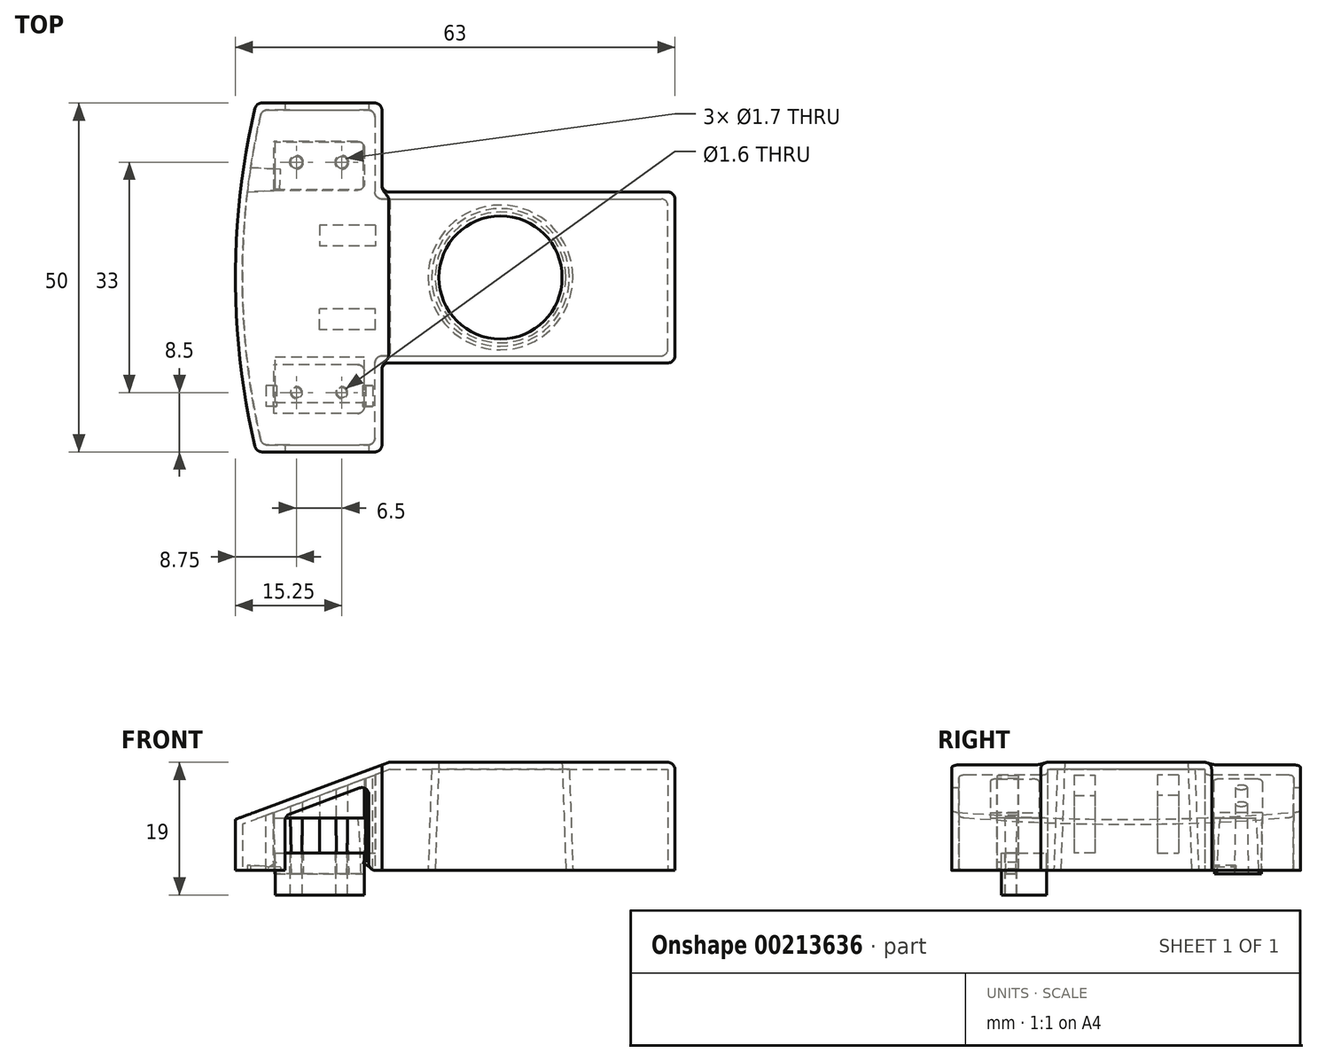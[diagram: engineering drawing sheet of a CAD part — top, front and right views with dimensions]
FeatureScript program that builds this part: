
annotation { "Feature Type Name" : "Feature", "Feature Type Description" : "" }
export const myFeature = defineFeature(function(context is Context, id is Id, definition is map)
    precondition{}
    {
        {
            var Q0;
            Q0=qCreatedBy(makeId("Top.planeOp"),FACE);
            var sketch = newSketch(context, id + "F0", { "sketchPlane" : qUnion([Q0])});
            skCircle(sketch, "E0", {"center": v(-4, 0) * mm, "radius": 9.37 * mm});
            skLineSegment(sketch, "E1.bottom", {"start": v(-21, -12.25) * mm, "end": v(21, -12.25) * mm});
            skLineSegment(sketch, "E1.top", {"start": v(-21, 12.25) * mm, "end": v(21, 12.25) * mm});
            skLineSegment(sketch, "E1.right", {"start": v(21, -12.25) * mm, "end": v(21, 12.25) * mm});
            skLineSegment(sketch, "E2.bottom", {"start": v(-21, -25) * mm, "end": v(-39, -25) * mm});
            skLineSegment(sketch, "E2.top", {"start": v(-21, 25) * mm, "end": v(-39, 25) * mm});
            skLineSegment(sketch, "E2.left", {"start": v(-21, -25) * mm, "end": v(-21, -12.25) * mm});
            skLineSegment(sketch, "E2.right", {"start": v(-39, -25) * mm, "end": v(-39, 25) * mm});
            skPoint(sketch, "E2.middle", {"position": v(-30, 0) * mm});
            skLineSegment(sketch, "E3.trimOffspring", {"start": v(-21, 12.25) * mm, "end": v(-21, 25) * mm});
            skLineSegment(sketch, "E4", {"start": v(-20, 12.25) * mm, "end": v(-20, -12.25) * mm});
            skPoint(sketch, "E5", {"position": v(-42, 0) * mm});
            skPoint(sketch, "E5.positionSnap0", {"position": v(-39, 0) * mm});
            skArc(sketch, "E6", {"start": v(-39, 25) * mm, "mid": v(-42, 0) * mm, "end": v(-39, -25) * mm});
            skSolve(sketch);
        }
        {
            var Q0;
            Q0=qSketchRegion(id+"F0",true);
            var Q1;
            Q1=makeQuery(id+"F0.imprint","IMPRINT",FACE,{"disambiguationData":[TD([[makeQuery(id+"F0.imprint","IMPRINT",EDGE,{"derivedFrom":sQuery(id+"F0.wireOp",EDGE,"E0")}),1.0]])]});
            extrude(context, id + "F1", {"entities" : qUnion([Q0, Q1]), "depth" : 15.5 * mm});
        }
        {
            var Q0;
            Q0=makeQuery(id+"F0.imprint","IMPRINT",FACE,{"disambiguationData":[TD([[makeQuery(id+"F0.imprint","IMPRINT",EDGE,{"derivedFrom":sQuery(id+"F0.wireOp",EDGE,"E0")}),1.0]])]});
            var Q1;
            Q1=makeQuery(id+"F1.opExtrude","CAP_FACE",FACE,{"disambiguationData":[OSD([sQuery(id+"F0.wireOp",EDGE,"E1.bottom"),sQuery(id+"F0.wireOp",EDGE,"E1.top"),sQuery(id+"F0.wireOp",EDGE,"E1.right"),sQuery(id+"F0.wireOp",EDGE,"E2.bottom"),sQuery(id+"F0.wireOp",EDGE,"E2.top"),sQuery(id+"F0.wireOp",EDGE,"E2.left"),sQuery(id+"F0.wireOp",EDGE,"E3.trimOffspring"),sQuery(id+"F0.wireOp",EDGE,"E6")])],"isStart":false});
            extrude(context, id + "F2", {"entities" : qUnion([Q0]), "operationType" : NewBodyOperationType.REMOVE, "endBound" : BoundingType.UP_TO_SURFACE, "endBoundEntityFace" : qUnion([Q1]), "depth" : 25 * mm, "hasDraft" : true, "draftAngle" : 2 * degree, "draftPullDirection" : true});
        }
        {
            var Q0;
            Q0=qCreatedBy(makeId("Front.planeOp"),FACE);
            var Q1;
            Q1=makeQuery(id+"F1.opExtrude","CAP_EDGE",EDGE,{"disambiguationData":[OSD([sQuery(id+"F0.wireOp",EDGE,"E2.bottom")])],"isStart":true});
            cPlane(context, id + "F3", {"entities" : qUnion([Q0, Q1]), "cplaneType" : CPlaneType.LINE_ANGLE, "offset" : 25 * mm, "angle" : 0 * degree, "width" : 150 * mm, "height" : 150 * mm});
        }
        {
            var Q0;
            Q0=qCreatedBy(id+"F3.planeOp",FACE);
            var sketch = newSketch(context, id + "F4", { "sketchPlane" : qUnion([Q0])});
            skLineSegment(sketch, "E7", {"start": v(20, 15.5) * mm, "end": v(42, 15.5) * mm});
            skLineSegment(sketch, "E8", {"start": v(42, 15.5) * mm, "end": v(42, 7.32) * mm});
            skLineSegment(sketch, "E9", {"start": v(42, 7.32) * mm, "end": v(20, 15.5) * mm});
            skLineSegment(sketch, "E10", {"start": v(42, 0) * mm, "end": v(41.46, 15.5) * mm, "construction": true});
            skLineSegment(sketch, "E11", {"start": v(42, 0) * mm, "end": v(42, 27.73) * mm, "construction": true});
            skSolve(sketch);
        }
        {
            var Q0;
            Q0=qSketchRegion(id+"F4",true);
            extrude(context, id + "F5", {"entities" : qUnion([Q0]), "operationType" : NewBodyOperationType.REMOVE, "endBound" : BoundingType.THROUGH_ALL, "depth" : 25 * mm});
        }
        {
            var Q0;
            Q0=makeQuery(id+"F1.opExtrude","CAP_FACE",FACE,{"disambiguationData":[OSD([sQuery(id+"F0.wireOp",EDGE,"E1.bottom"),sQuery(id+"F0.wireOp",EDGE,"E1.top"),sQuery(id+"F0.wireOp",EDGE,"E1.right"),sQuery(id+"F0.wireOp",EDGE,"E2.bottom"),sQuery(id+"F0.wireOp",EDGE,"E2.top"),sQuery(id+"F0.wireOp",EDGE,"E2.left"),sQuery(id+"F0.wireOp",EDGE,"E3.trimOffspring"),sQuery(id+"F0.wireOp",EDGE,"E6")])],"isStart":true});
            shell(context, id + "F6", {"entities" : qUnion([Q0]), "thickness" : 1 * mm});
        }
        {
            var Q0;
            Q0=makeQuery(id+"F1.opExtrude","SWEPT_FACE",FACE,{"disambiguationData":[OSD([sQuery(id+"F0.wireOp",EDGE,"E2.bottom")])]});
            var sketch = newSketch(context, id + "F7", { "sketchPlane" : qUnion([Q0])});
            skLineSegment(sketch, "E12", {"start": v(-20, 15.5) * mm, "end": v(-39, 8.43) * mm});
            skLineSegment(sketch, "E13", {"start": v(-39, 8.43) * mm, "end": v(-39, 15.5) * mm});
            skLineSegment(sketch, "E14", {"start": v(-39, 15.5) * mm, "end": v(-20, 15.5) * mm});
            skLineSegment(sketch, "E15", {"start": v(-34.87, 0) * mm, "end": v(-34.87, 7.86) * mm});
            skLineSegment(sketch, "E16", {"start": v(-34.87, 7.86) * mm, "end": v(-22.87, 12.32) * mm});
            skLineSegment(sketch, "E17", {"start": v(-22.87, 0) * mm, "end": v(-34.87, 0) * mm});
            skLineSegment(sketch, "E18", {"start": v(-22.87, 12.32) * mm, "end": v(-22.87, 0) * mm});
            skSolve(sketch);
        }
        {
            var Q0;
            Q0=makeQuery(id+"F7.imprint","IMPRINT",FACE,{"disambiguationData":[TD([[makeQuery(id+"F7.imprint","IMPRINT",EDGE,{"derivedFrom":sQuery(id+"F7.wireOp",EDGE,"E15")}),-1.0]])]});
            extrude(context, id + "F8", {"entities" : qUnion([Q0]), "operationType" : NewBodyOperationType.REMOVE, "endBound" : BoundingType.THROUGH_ALL, "oppositeDirection" : true, "depth" : 25 * mm});
        }
        {
            var Q0;
            Q0=makeQuery(id+"F1.opExtrude","CAP_FACE",FACE,{"disambiguationData":[OSD([sQuery(id+"F0.wireOp",EDGE,"E0"),sQuery(id+"F0.wireOp",EDGE,"E1.bottom"),sQuery(id+"F0.wireOp",EDGE,"E1.top"),sQuery(id+"F0.wireOp",EDGE,"E1.right"),sQuery(id+"F0.wireOp",EDGE,"E2.bottom"),sQuery(id+"F0.wireOp",EDGE,"E2.top"),sQuery(id+"F0.wireOp",EDGE,"E2.left"),sQuery(id+"F0.wireOp",EDGE,"E2.right"),sQuery(id+"F0.wireOp",EDGE,"E3.trimOffspring")])],"isStart":false});
            cPlane(context, id + "F9", {"entities" : qUnion([Q0]), "cplaneType" : CPlaneType.OFFSET, "offset" : 8 * mm, "oppositeDirection" : true, "width" : 150 * mm, "height" : 150 * mm});
        }
        {
            var Q0;
            Q0=qCreatedBy(id+"F9.planeOp",FACE);
            var sketch = newSketch(context, id + "F10", { "sketchPlane" : qUnion([Q0])});
            skLineSegment(sketch, "E19", {"start": v(0, 0) * mm, "end": v(-63, 0) * mm, "construction": true});
            skLineSegment(sketch, "E20.bottom", {"start": v(-36.5, -12.5) * mm, "end": v(-23.5, -12.5) * mm});
            skLineSegment(sketch, "E20.top", {"start": v(-36.5, -19.5) * mm, "end": v(-23.5, -19.5) * mm});
            skLineSegment(sketch, "E20.left", {"start": v(-36.5, -12.5) * mm, "end": v(-36.5, -19.5) * mm});
            skLineSegment(sketch, "E20.right", {"start": v(-23.5, -12.5) * mm, "end": v(-23.5, -19.5) * mm});
            skPoint(sketch, "E20.middle", {"position": v(-30, -16) * mm});
            skPoint(sketch, "E21", {"position": v(-33.25, -16.5) * mm});
            skPoint(sketch, "E22", {"position": v(-26.75, -16.5) * mm});
            skCircle(sketch, "E23", {"center": v(-33.25, -16.5) * mm, "radius": 0.85 * mm});
            skCircle(sketch, "E24", {"center": v(-26.75, -16.5) * mm, "radius": 0.85 * mm});
            skLineSegment(sketch, "E25.MirrorCS", {"start": v(-36.5, 12.5) * mm, "end": v(-23.5, 12.5) * mm});
            skLineSegment(sketch, "E26.MirrorCS", {"start": v(-36.5, 12.5) * mm, "end": v(-36.5, 19.5) * mm});
            skLineSegment(sketch, "E27.MirrorCS", {"start": v(-36.5, 19.5) * mm, "end": v(-23.5, 19.5) * mm});
            skLineSegment(sketch, "E28.MirrorCS", {"start": v(-23.5, 12.5) * mm, "end": v(-23.5, 19.5) * mm});
            skCircle(sketch, "E29.MirrorC", {"center": v(-26.75, 16.5) * mm, "radius": 0.85 * mm});
            skCircle(sketch, "E30.MirrorC", {"center": v(-33.25, 16.5) * mm, "radius": 0.85 * mm});
            skSolve(sketch);
        }
        {
            var Q0;
            Q0=makeQuery(id+"F10.imprint","IMPRINT",FACE,{"disambiguationData":[TD([[makeQuery(id+"F10.imprint","IMPRINT",EDGE,{"derivedFrom":sQuery(id+"F10.wireOp",EDGE,"E20.bottom")}),-1.0]])]});
            var Q1;
            Q1=makeQuery(id+"F10.imprint","IMPRINT",FACE,{"disambiguationData":[TD([[makeQuery(id+"F10.imprint","IMPRINT",EDGE,{"derivedFrom":sQuery(id+"F10.wireOp",EDGE,"E23")}),1.0]])]});
            var Q2;
            Q2=makeQuery(id+"F10.imprint","IMPRINT",FACE,{"disambiguationData":[TD([[makeQuery(id+"F10.imprint","IMPRINT",EDGE,{"derivedFrom":sQuery(id+"F10.wireOp",EDGE,"E24")}),1.0]])]});
            var Q3;
            Q3=makeQuery(id+"F10.imprint","IMPRINT",FACE,{"disambiguationData":[TD([[makeQuery(id+"F10.imprint","IMPRINT",EDGE,{"derivedFrom":sQuery(id+"F10.wireOp",EDGE,"E25.MirrorCS")}),1.0]])]});
            var Q4;
            Q4=makeQuery(id+"F10.imprint","IMPRINT",FACE,{"disambiguationData":[TD([[makeQuery(id+"F10.imprint","IMPRINT",EDGE,{"derivedFrom":sQuery(id+"F10.wireOp",EDGE,"E30.MirrorC")}),-1.0]])]});
            var Q5;
            Q5=makeQuery(id+"F10.imprint","IMPRINT",FACE,{"disambiguationData":[TD([[makeQuery(id+"F10.imprint","IMPRINT",EDGE,{"derivedFrom":sQuery(id+"F10.wireOp",EDGE,"E29.MirrorC")}),-1.0]])]});
            var Q6;
            Q6=makeQuery(id+"F6.opShell","OFFSET_FACE",FACE,{"disambiguationData":[OSD([sQuery(id+"F4.wireOp",EDGE,"E9")])]});
            extrude(context, id + "F11", {"entities" : qUnion([Q0, Q1, Q2, Q3, Q4, Q5]), "operationType" : NewBodyOperationType.ADD, "endBound" : BoundingType.UP_TO_SURFACE, "endBoundEntityFace" : qUnion([Q6]), "depth" : 25 * mm});
        }
        {
            var Q0;
            Q0=makeQuery(id+"F10.imprint","IMPRINT",FACE,{"disambiguationData":[TD([[makeQuery(id+"F10.imprint","IMPRINT",EDGE,{"derivedFrom":sQuery(id+"F10.wireOp",EDGE,"E23")}),1.0]])]});
            var Q1;
            Q1=makeQuery(id+"F10.imprint","IMPRINT",FACE,{"disambiguationData":[TD([[makeQuery(id+"F10.imprint","IMPRINT",EDGE,{"derivedFrom":sQuery(id+"F10.wireOp",EDGE,"E29.MirrorC")}),-1.0]])]});
            var Q2;
            Q2=makeQuery(id+"F10.imprint","IMPRINT",FACE,{"disambiguationData":[TD([[makeQuery(id+"F10.imprint","IMPRINT",EDGE,{"derivedFrom":sQuery(id+"F10.wireOp",EDGE,"E30.MirrorC")}),-1.0]])]});
            var Q3;
            Q3=makeQuery(id+"F10.imprint","IMPRINT",FACE,{"disambiguationData":[TD([[makeQuery(id+"F10.imprint","IMPRINT",EDGE,{"derivedFrom":sQuery(id+"F10.wireOp",EDGE,"E24")}),1.0]])]});
            extrude(context, id + "F12", {"entities" : qUnion([Q0, Q1, Q2, Q3]), "operationType" : NewBodyOperationType.ADD, "oppositeDirection" : true, "depth" : 8 * mm, "hasDraft" : true, "draftAngle" : 1 * degree, "draftPullDirection" : true});
        }
        {
            var Q0;
            Q0=makeQuery(id+"F1.opExtrude","CAP_EDGE",EDGE,{"disambiguationData":[OSD([sQuery(id+"F0.wireOp",EDGE,"E1.bottom")])],"isStart":false});
            var Q1;
            Q1=makeQuery(id+"F1.opExtrude","CAP_EDGE",EDGE,{"disambiguationData":[OSD([sQuery(id+"F0.wireOp",EDGE,"E1.right")])],"isStart":false});
            var Q2;
            Q2=makeQuery(id+"F1.opExtrude","CAP_EDGE",EDGE,{"disambiguationData":[OSD([sQuery(id+"F0.wireOp",EDGE,"E1.top")])],"isStart":false});
            var Q3;
            Q3=makeQuery(id+"F1.opExtrude","SWEPT_EDGE",EDGE,{"disambiguationData":[OSD([sQuery(id+"F0.wireOp",EDGE,"E1.bottom"),sQuery(id+"F0.wireOp",EDGE,"E1.right")])]});
            var Q4;
            Q4=makeQuery(id+"F1.opExtrude","SWEPT_EDGE",EDGE,{"disambiguationData":[OSD([sQuery(id+"F0.wireOp",EDGE,"E1.top"),sQuery(id+"F0.wireOp",EDGE,"E1.right")])]});
            fillet(context, id + "F13", {"entities" : qUnion([Q0, Q1, Q2, Q3, Q4]), "radius" : 1 * mm, "tangentPropagation" : true, "allowEdgeOverflow" : false});
        }
        {
            var Q0;
            Q0=makeQuery(id+"F1.opExtrude","SWEPT_EDGE",EDGE,{"disambiguationData":[OSD([sQuery(id+"F0.wireOp",EDGE,"E2.bottom"),sQuery(id+"F0.wireOp",EDGE,"E2.left")])]});
            var Q1;
            Q1=makeQuery(id+"F5.boolean.opBoolean","INTERSECT",EDGE,{"derivedFrom":[makeQuery(id+"F1.opExtrude","SWEPT_FACE",FACE,{"disambiguationData":[OSD([sQuery(id+"F0.wireOp",EDGE,"E2.left")])]}),makeQuery(id+"F5.opExtrude","SWEPT_FACE",FACE,{"disambiguationData":[OSD([sQuery(id+"FjstzwEYRuGCUyq_1.wireOp",EDGE,"6156deb2-2619-4c56-9df6-34b3699534c4")])]})]});
            var Q2;
            Q2=makeQuery(id+"F5.boolean.opBoolean","COPY",EDGE,{"derivedFrom":makeQuery(id+"F5.opExtrude","CAP_EDGE",EDGE,{"disambiguationData":[OSD([sQuery(id+"FjstzwEYRuGCUyq_1.wireOp",EDGE,"6156deb2-2619-4c56-9df6-34b3699534c4")])],"isStart":true})});
            var Q3;
            Q3=makeQuery(id+"F1.opExtrude","SWEPT_EDGE",EDGE,{"disambiguationData":[OSD([sQuery(id+"F0.wireOp",EDGE,"E2.bottom"),sQuery(id+"F0.wireOp",EDGE,"E2.right"),sQuery(id+"F0.wireOp",EDGE,"E6")])]});
            var Q4;
            Q4=makeQuery(id+"F5.boolean.opBoolean","INTERSECT",EDGE,{"derivedFrom":[makeQuery(id+"F1.opExtrude","SWEPT_FACE",FACE,{"disambiguationData":[OSD([sQuery(id+"F0.wireOp",EDGE,"E6")])]}),makeQuery(id+"F5.opExtrude","SWEPT_FACE",FACE,{"disambiguationData":[OSD([sQuery(id+"FjstzwEYRuGCUyq_1.wireOp",EDGE,"6156deb2-2619-4c56-9df6-34b3699534c4")])]})]});
            var Q5;
            Q5=makeQuery(id+"F5.boolean.opBoolean","INTERSECT",EDGE,{"derivedFrom":[makeQuery(id+"F1.opExtrude","SWEPT_FACE",FACE,{"disambiguationData":[OSD([sQuery(id+"F0.wireOp",EDGE,"E2.top")])]}),makeQuery(id+"F5.opExtrude","SWEPT_FACE",FACE,{"disambiguationData":[OSD([sQuery(id+"FjstzwEYRuGCUyq_1.wireOp",EDGE,"6156deb2-2619-4c56-9df6-34b3699534c4")])]})]});
            var Q6;
            Q6=makeQuery(id+"F1.opExtrude","SWEPT_EDGE",EDGE,{"disambiguationData":[OSD([sQuery(id+"F0.wireOp",EDGE,"E2.top"),sQuery(id+"F0.wireOp",EDGE,"E2.right"),sQuery(id+"F0.wireOp",EDGE,"E6")])]});
            var Q7;
            Q7=makeQuery(id+"F1.opExtrude","SWEPT_EDGE",EDGE,{"disambiguationData":[OSD([sQuery(id+"F0.wireOp",EDGE,"E2.top"),sQuery(id+"F0.wireOp",EDGE,"E3.trimOffspring")])]});
            var Q8;
            Q8=makeQuery(id+"F5.boolean.opBoolean","INTERSECT",EDGE,{"derivedFrom":[makeQuery(id+"F1.opExtrude","SWEPT_FACE",FACE,{"disambiguationData":[OSD([sQuery(id+"F0.wireOp",EDGE,"E3.trimOffspring")])]}),makeQuery(id+"F5.opExtrude","SWEPT_FACE",FACE,{"disambiguationData":[OSD([sQuery(id+"FjstzwEYRuGCUyq_1.wireOp",EDGE,"6156deb2-2619-4c56-9df6-34b3699534c4")])]})]});
            fillet(context, id + "F14", {"entities" : qUnion([Q0, Q1, Q2, Q3, Q4, Q5, Q6, Q7, Q8]), "radius" : 1 * mm, "tangentPropagation" : true, "allowEdgeOverflow" : false});
        }
        {
            var Q0;
            Q0=makeQuery(id+"F1.opExtrude","SWEPT_EDGE",EDGE,{"disambiguationData":[OSD([sQuery(id+"F0.wireOp",EDGE,"E1.top"),sQuery(id+"F0.wireOp",EDGE,"E3.trimOffspring")])]});
            fillet(context, id + "F15", {"entities" : qUnion([Q0]), "radius" : 1 * mm, "tangentPropagation" : true, "allowEdgeOverflow" : false});
        }
        {
            var Q0;
            Q0=makeQuery(id+"F1.opExtrude","SWEPT_EDGE",EDGE,{"disambiguationData":[OSD([sQuery(id+"F0.wireOp",EDGE,"E1.bottom"),sQuery(id+"F0.wireOp",EDGE,"E2.left")])]});
            var Q1;
            {var subQ0=sQuery(id+"F0.wireOp",EDGE,"E2.bottom");var subQ1=sQuery(id+"F7.wireOp",EDGE,"E18");Q1=makeQuery(id+"F8.boolean.opBoolean","COPY",EDGE,{"disambiguationData":[TD([makeQuery(id+"F1.opExtrude","SWEPT_FACE",FACE,{"disambiguationData":[OSD([subQ0])]})])],"derivedFrom":makeQuery(id+"F8.opExtrude","SWEPT_EDGE",EDGE,{"disambiguationData":[OSD([subQ0,sQuery(id+"F7.wireOp",EDGE,"E17"),subQ1])]})});}
            var Q2;
            {var subQ0=sQuery(id+"F0.wireOp",EDGE,"E2.bottom");var subQ1=sQuery(id+"F7.wireOp",EDGE,"E15");Q2=makeQuery(id+"F8.boolean.opBoolean","COPY",EDGE,{"disambiguationData":[TD([makeQuery(id+"F1.opExtrude","SWEPT_FACE",FACE,{"disambiguationData":[OSD([subQ0])]})])],"derivedFrom":makeQuery(id+"F8.opExtrude","SWEPT_EDGE",EDGE,{"disambiguationData":[OSD([subQ0,subQ1,sQuery(id+"F7.wireOp",EDGE,"E17")])]})});}
            var Q3;
            {var subQ0=sQuery(id+"F0.wireOp",EDGE,"E2.top");var subQ1=sQuery(id+"F0.wireOp",EDGE,"E2.bottom");var subQ2=sQuery(id+"F7.wireOp",EDGE,"E15");Q3=makeQuery(id+"F8.boolean.opBoolean","COPY",EDGE,{"disambiguationData":[TD([makeQuery(id+"F1.opExtrude","SWEPT_FACE",FACE,{"disambiguationData":[OSD([subQ0])]})])],"derivedFrom":makeQuery(id+"F8.opExtrude","SWEPT_EDGE",EDGE,{"disambiguationData":[OSD([subQ1,subQ2,sQuery(id+"F7.wireOp",EDGE,"E17")])]})});}
            var Q4;
            {var subQ0=sQuery(id+"F0.wireOp",EDGE,"E2.top");var subQ1=sQuery(id+"F0.wireOp",EDGE,"E2.bottom");var subQ2=sQuery(id+"F7.wireOp",EDGE,"E18");Q4=makeQuery(id+"F8.boolean.opBoolean","COPY",EDGE,{"disambiguationData":[TD([makeQuery(id+"F1.opExtrude","SWEPT_FACE",FACE,{"disambiguationData":[OSD([subQ0])]})])],"derivedFrom":makeQuery(id+"F8.opExtrude","SWEPT_EDGE",EDGE,{"disambiguationData":[OSD([subQ1,sQuery(id+"F7.wireOp",EDGE,"E17"),subQ2])]})});}
            var Q5;
            {var subQ0=sQuery(id+"F0.wireOp",EDGE,"E2.top");var subQ1=sQuery(id+"F7.wireOp",EDGE,"E18");var subQ2=sQuery(id+"F7.wireOp",EDGE,"E16");Q5=makeQuery(id+"F8.boolean.opBoolean","COPY",EDGE,{"disambiguationData":[TD([makeQuery(id+"F1.opExtrude","SWEPT_FACE",FACE,{"disambiguationData":[OSD([subQ0])]})])],"derivedFrom":makeQuery(id+"F8.opExtrude","SWEPT_EDGE",EDGE,{"disambiguationData":[OSD([subQ2,subQ1])]})});}
            var Q6;
            {var subQ0=sQuery(id+"F0.wireOp",EDGE,"E2.top");var subQ1=sQuery(id+"F7.wireOp",EDGE,"E15");var subQ2=sQuery(id+"F7.wireOp",EDGE,"E16");Q6=makeQuery(id+"F8.boolean.opBoolean","COPY",EDGE,{"disambiguationData":[TD([makeQuery(id+"F1.opExtrude","SWEPT_FACE",FACE,{"disambiguationData":[OSD([subQ0])]})])],"derivedFrom":makeQuery(id+"F8.opExtrude","SWEPT_EDGE",EDGE,{"disambiguationData":[OSD([subQ1,subQ2])]})});}
            var Q7;
            {var subQ0=sQuery(id+"F0.wireOp",EDGE,"E2.bottom");var subQ1=sQuery(id+"F7.wireOp",EDGE,"E18");var subQ2=sQuery(id+"F7.wireOp",EDGE,"E16");Q7=makeQuery(id+"F8.boolean.opBoolean","COPY",EDGE,{"disambiguationData":[TD([makeQuery(id+"F1.opExtrude","SWEPT_FACE",FACE,{"disambiguationData":[OSD([subQ0])]})])],"derivedFrom":makeQuery(id+"F8.opExtrude","SWEPT_EDGE",EDGE,{"disambiguationData":[OSD([subQ2,subQ1])]})});}
            var Q8;
            {var subQ0=sQuery(id+"F0.wireOp",EDGE,"E2.bottom");var subQ1=sQuery(id+"F7.wireOp",EDGE,"E15");var subQ2=sQuery(id+"F7.wireOp",EDGE,"E16");Q8=makeQuery(id+"F8.boolean.opBoolean","COPY",EDGE,{"disambiguationData":[TD([makeQuery(id+"F1.opExtrude","SWEPT_FACE",FACE,{"disambiguationData":[OSD([subQ0])]})])],"derivedFrom":makeQuery(id+"F8.opExtrude","SWEPT_EDGE",EDGE,{"disambiguationData":[OSD([subQ1,subQ2])]})});}
            var Q9;
            Q9=makeQuery(id+"F6.opShell","OFFSET_EDGE",EDGE,{"disambiguationData":[OSD([sQuery(id+"F0.wireOp",EDGE,"E1.top"),sQuery(id+"F0.wireOp",EDGE,"E3.trimOffspring")])]});
            var Q10;
            Q10=makeQuery(id+"F6.opShell","OFFSET_EDGE",EDGE,{"disambiguationData":[OSD([sQuery(id+"F0.wireOp",EDGE,"E1.bottom"),sQuery(id+"F0.wireOp",EDGE,"E2.left")])]});
            fillet(context, id + "F16", {"entities" : qUnion([Q0, Q1, Q2, Q3, Q4, Q5, Q6, Q7, Q8, Q9, Q10]), "radius" : 1 * mm, "tangentPropagation" : true, "allowEdgeOverflow" : false});
        }
        {
            var Q0;
            Q0=makeQuery(id+"F6.opShell","OFFSET_EDGE",EDGE,{"disambiguationData":[OSD([sQuery(id+"F0.wireOp",EDGE,"E1.top"),sQuery(id+"F0.wireOp",EDGE,"E1.right")])]});
            var Q1;
            Q1=makeQuery(id+"F6.opShell","OFFSET_EDGE",EDGE,{"disambiguationData":[OSD([sQuery(id+"F0.wireOp",EDGE,"E1.bottom"),sQuery(id+"F0.wireOp",EDGE,"E1.right")])]});
            var Q2;
            {var subQ0=sQuery(id+"F0.wireOp",EDGE,"E0");Q2=makeQuery(id+"F6.opShell","OFFSET_EDGE",EDGE,{"disambiguationData":[OSD([subQ0]),TDD([makeQuery(id+"F1.opExtrude","CAP_EDGE",EDGE,{"disambiguationData":[OSD([subQ0])],"isStart":false})])]});}
            var Q3;
            Q3=makeQuery(id+"F6.opShell","OFFSET_EDGE",EDGE,{"disambiguationData":[OSD([sQuery(id+"F0.wireOp",EDGE,"E2.top"),sQuery(id+"F0.wireOp",EDGE,"E3.trimOffspring")])]});
            var Q4;
            Q4=makeQuery(id+"F6.opShell","OFFSET_EDGE",EDGE,{"disambiguationData":[OSD([sQuery(id+"F0.wireOp",EDGE,"E2.top"),sQuery(id+"F0.wireOp",EDGE,"E2.right"),sQuery(id+"F0.wireOp",EDGE,"E6")])]});
            var Q5;
            Q5=makeQuery(id+"F6.opShell","OFFSET_EDGE",EDGE,{"disambiguationData":[OSD([sQuery(id+"F0.wireOp",EDGE,"E2.bottom"),sQuery(id+"F0.wireOp",EDGE,"E2.left")])]});
            var Q6;
            Q6=makeQuery(id+"F6.opShell","OFFSET_EDGE",EDGE,{"disambiguationData":[OSD([sQuery(id+"F0.wireOp",EDGE,"E2.bottom"),sQuery(id+"F0.wireOp",EDGE,"E2.right"),sQuery(id+"F0.wireOp",EDGE,"E6")])]});
            var Q7;
            Q7=makeQuery(id+"F11.opExtrude","SWEPT_EDGE",EDGE,{"disambiguationData":[OSD([sQuery(id+"F10.wireOp",EDGE,"E20.bottom"),sQuery(id+"F10.wireOp",EDGE,"E20.right")])]});
            var Q8;
            Q8=makeQuery(id+"F11.opExtrude","SWEPT_EDGE",EDGE,{"disambiguationData":[OSD([sQuery(id+"F10.wireOp",EDGE,"E20.top"),sQuery(id+"F10.wireOp",EDGE,"E20.right")])]});
            var Q9;
            Q9=makeQuery(id+"F11.opExtrude","SWEPT_EDGE",EDGE,{"disambiguationData":[OSD([sQuery(id+"F10.wireOp",EDGE,"E27.MirrorCS"),sQuery(id+"F10.wireOp",EDGE,"E28.MirrorCS")])]});
            var Q10;
            Q10=makeQuery(id+"F11.opExtrude","SWEPT_EDGE",EDGE,{"disambiguationData":[OSD([sQuery(id+"F10.wireOp",EDGE,"E25.MirrorCS"),sQuery(id+"F10.wireOp",EDGE,"E28.MirrorCS")])]});
            fillet(context, id + "F17", {"entities" : qUnion([Q0, Q1, Q2, Q3, Q4, Q5, Q6, Q7, Q8, Q9, Q10]), "radius" : 1 * mm, "tangentPropagation" : true, "allowEdgeOverflow" : false});
        }
        {
            var Q0;
            Q0=qCreatedBy(id+"F9.planeOp",FACE);
            var sketch = newSketch(context, id + "F18", { "sketchPlane" : qUnion([Q0])});
            skPoint(sketch, "E31", {"position": v(-29.94, -4.5) * mm});
            skLineSegment(sketch, "E32.bottom", {"start": v(-29.94, -4.5) * mm, "end": v(-21.94, -4.5) * mm});
            skLineSegment(sketch, "E32.top", {"start": v(-29.94, -7.5) * mm, "end": v(-21.94, -7.5) * mm});
            skLineSegment(sketch, "E32.left", {"start": v(-29.94, -4.5) * mm, "end": v(-29.94, -7.5) * mm});
            skLineSegment(sketch, "E32.right", {"start": v(-21.94, -4.5) * mm, "end": v(-21.94, -7.5) * mm});
            skLineSegment(sketch, "E33", {"start": v(0, 0) * mm, "end": v(-48.4, 0) * mm, "construction": true});
            skLineSegment(sketch, "E34.MirrorCS", {"start": v(-29.94, 4.5) * mm, "end": v(-21.94, 4.5) * mm});
            skLineSegment(sketch, "E35.MirrorCS", {"start": v(-21.94, 4.5) * mm, "end": v(-21.94, 7.5) * mm});
            skLineSegment(sketch, "E36.MirrorCS", {"start": v(-29.94, 7.5) * mm, "end": v(-21.94, 7.5) * mm});
            skLineSegment(sketch, "E37.MirrorCS", {"start": v(-29.94, 4.5) * mm, "end": v(-29.94, 7.5) * mm});
            skSolve(sketch);
        }
        {
            var Q0;
            Q0=qSketchRegion(id+"F18",true);
            var Q1;
            Q1=makeQuery(id+"F6.opShell","OFFSET_FACE",FACE,{"disambiguationData":[OSD([sQuery(id+"F4.wireOp",EDGE,"E9")])]});
            extrude(context, id + "F19", {"entities" : qUnion([Q0]), "operationType" : NewBodyOperationType.ADD, "endBound" : BoundingType.UP_TO_SURFACE, "endBoundEntityFace" : qUnion([Q1]), "depth" : 25 * mm, "hasSecondDirection" : true, "secondDirectionOppositeDirection" : true, "secondDirectionDepth" : 5 * mm});
        }
        {
            var Q0;
            Q0=makeQuery(id+"F11.opExtrude","CAP_FACE",FACE,{"disambiguationData":[OSD([sQuery(id+"F10.wireOp",EDGE,"E20.bottom"),sQuery(id+"F10.wireOp",EDGE,"E20.top"),sQuery(id+"F10.wireOp",EDGE,"E20.left"),sQuery(id+"F10.wireOp",EDGE,"E20.right")])],"isStart":true});
            cPlane(context, id + "F20", {"entities" : qUnion([Q0]), "cplaneType" : CPlaneType.OFFSET, "offset" : 5 * mm, "width" : 150 * mm, "height" : 150 * mm});
        }
        {
            var Q0;
            Q0=qCreatedBy(id+"F20.planeOp",FACE);
            var sketch = newSketch(context, id + "F21", { "sketchPlane" : qUnion([Q0])});
            skLineSegment(sketch, "E38.bottom", {"start": v(-36.3, 17.9) * mm, "end": v(-23.5, 17.9) * mm});
            skLineSegment(sketch, "E38.top", {"start": v(-36.3, 11.4) * mm, "end": v(-23.5, 11.4) * mm});
            skLineSegment(sketch, "E38.left", {"start": v(-36.3, 17.9) * mm, "end": v(-36.3, 11.4) * mm});
            skLineSegment(sketch, "E38.right", {"start": v(-23.5, 17.9) * mm, "end": v(-23.5, 11.4) * mm});
            skCircle(sketch, "E39", {"center": v(-33.25, 16.5) * mm, "radius": 0.85 * mm});
            skCircle(sketch, "E40", {"center": v(-26.75, 16.5) * mm, "radius": 0.8 * mm});
            skSolve(sketch);
        }
        {
            var Q0;
            Q0 = qSketchRegion(id + "F21", true);
            extrude(context, id + "F22", {"entities" : qUnion([Q0]), "operationType" : NewBodyOperationType.ADD, "depth" : 6 * mm});
        }
        {
            var Q0;
            Q0=makeQuery(id+"F11.opExtrude","SWEPT_FACE",FACE,{"disambiguationData":[OSD([sQuery(id+"F10.wireOp",EDGE,"E20.top")])]});
            cPlane(context, id + "F23", {"entities" : qUnion([Q0]), "cplaneType" : CPlaneType.OFFSET, "offset" : 1 * mm, "oppositeDirection" : true, "width" : 150 * mm, "height" : 150 * mm});
        }
        {
            var Q0;
            Q0=qCreatedBy(id+"F23.planeOp",FACE);
            var sketch = newSketch(context, id + "F24", { "sketchPlane" : qUnion([Q0])});
            skLineSegment(sketch, "E41", {"start": v(-23.3, 13.2) * mm, "end": v(-23.3, 1.2) * mm});
            skLineSegment(sketch, "E42", {"start": v(-22.3, 1.2) * mm, "end": v(-22.3, 13.58) * mm});
            skLineSegment(sketch, "E43", {"start": v(-22.3, 13.58) * mm, "end": v(-23.3, 13.2) * mm});
            skLineSegment(sketch, "E44", {"start": v(-23.3, 1.2) * mm, "end": v(-23.8, 1.2) * mm});
            skLineSegment(sketch, "E45", {"start": v(-23.8, 1.2) * mm, "end": v(-22.3, 0.2) * mm});
            skLineSegment(sketch, "E46", {"start": v(-22.3, 0.2) * mm, "end": v(-22.3, 1.2) * mm});
            skLineSegment(sketch, "E47", {"start": v(-29.94, 13.18) * mm, "end": v(-29.94, -1.43) * mm, "construction": true});
            skLineSegment(sketch, "E48.MirrorCS", {"start": v(-36.09, 1.2) * mm, "end": v(-37.59, 0.2) * mm});
            skLineSegment(sketch, "E49.MirrorCS", {"start": v(-37.59, 0.2) * mm, "end": v(-37.59, 1.2) * mm});
            skLineSegment(sketch, "E50.MirrorCS", {"start": v(-37.59, 1.2) * mm, "end": v(-37.59, 13.58) * mm});
            skLineSegment(sketch, "E51.MirrorCS", {"start": v(-36.59, 13.2) * mm, "end": v(-36.59, 1.2) * mm});
            skLineSegment(sketch, "E52.MirrorCS", {"start": v(-36.59, 1.2) * mm, "end": v(-36.09, 1.2) * mm});
            skLineSegment(sketch, "E53", {"start": v(-36.59, 8.26) * mm, "end": v(-37.8, 7.82) * mm});
            skSolve(sketch);
        }
        {
            var Q0;
            Q0 = qSketchRegion(id + "F24", true);
            extrude(context, id + "F25", {"entities" : qUnion([Q0]), "oppositeDirection" : true, "depth" : 3 * mm});
        }
        {
            var Q0;
            Q0=makeQuery(id+"F11.opExtrude","SWEPT_FACE",FACE,{"disambiguationData":[OSD([sQuery(id+"F10.wireOp",EDGE,"E26.MirrorCS")])]});
            cPlane(context, id + "F26", {"entities" : qUnion([Q0]), "cplaneType" : CPlaneType.OFFSET, "offset" : 1 * mm, "oppositeDirection" : true, "width" : 150 * mm, "height" : 150 * mm});
        }
        {
            var Q0;
            Q0=qCreatedBy(id+"F26.planeOp",FACE);
            var sketch = newSketch(context, id + "F27", { "sketchPlane" : qUnion([Q0])});
            skLineSegment(sketch, "E54.bottom", {"start": v(-12.5, 0.5) * mm, "end": v(-15.5, 0.5) * mm});
            skLineSegment(sketch, "E54.top", {"start": v(-12.5, 0) * mm, "end": v(-15.5, 0) * mm});
            skLineSegment(sketch, "E54.left", {"start": v(-12.5, 0.5) * mm, "end": v(-12.5, 0) * mm});
            skLineSegment(sketch, "E54.right", {"start": v(-15.5, 0.5) * mm, "end": v(-15.5, 0) * mm});
            skSolve(sketch);
        }
        {
            var Q0;
            Q0 = qSketchRegion(id + "F27", true);
            var Q1;
            Q1=makeQuery(id+"F6.opShell","OFFSET_FACE",FACE,{"disambiguationData":[OSD([sQuery(id+"F0.wireOp",EDGE,"E6")])]});
            extrude(context, id + "F28", {"entities" : qUnion([Q0]), "operationType" : NewBodyOperationType.ADD, "endBound" : BoundingType.UP_TO_SURFACE, "endBoundEntityFace" : qUnion([Q1]), "depth" : 25 * mm, "hasDraft" : true, "draftAngle" : 3 * degree});
        }
        {
            var Q0;
            Q0=makeQuery(id+"F28.opExtrude","SWEPT_FACE",FACE,{"disambiguationData":[OSD([sQuery(id+"F27.wireOp",EDGE,"E54.right")])]});
            var sketch = newSketch(context, id + "F29", { "sketchPlane" : qUnion([Q0])});
            skLineSegment(sketch, "E55", {"start": v(36.26, 0) * mm, "end": v(41.08, 0) * mm});
            skLineSegment(sketch, "E56", {"start": v(36.26, 0) * mm, "end": v(41.2, -0.57) * mm});
            skLineSegment(sketch, "E57", {"start": v(41.2, -0.57) * mm, "end": v(41.08, 0) * mm});
            skSolve(sketch);
        }
        {
            var Q0;
            Q0 = qSketchRegion(id + "F29", true);
            extrude(context, id + "F30", {"entities" : qUnion([Q0]), "operationType" : NewBodyOperationType.REMOVE, "oppositeDirection" : true, "depth" : 7 * mm});
        }
    });
